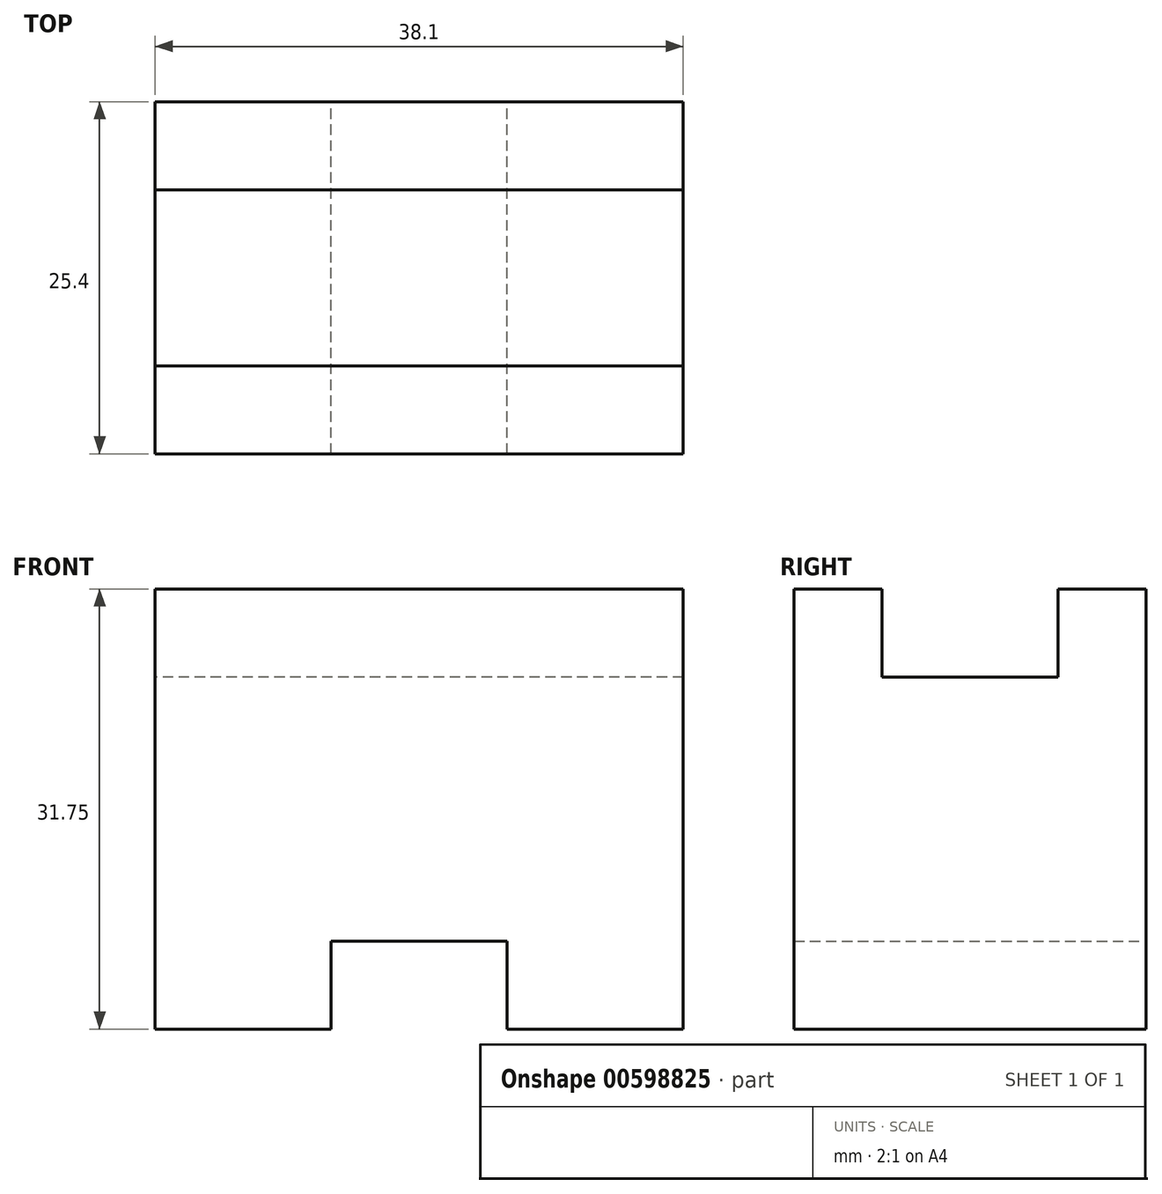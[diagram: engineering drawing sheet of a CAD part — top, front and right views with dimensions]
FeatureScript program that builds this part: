
annotation { "Feature Type Name" : "Feature", "Feature Type Description" : "" }
export const myFeature = defineFeature(function(context is Context, id is Id, definition is map)
    precondition{}
    {
        {
            var Q0;
            Q0=qCreatedBy(makeId("Front.planeOp"),FACE);
            var sketch = newSketch(context, id + "F0", { "sketchPlane" : qUnion([Q0])});
            skLineSegment(sketch, "E0", {"start": v(0, 0) * mm, "end": v(0, 31.75) * mm});
            skLineSegment(sketch, "E1", {"start": v(0, 31.75) * mm, "end": v(38.1, 31.75) * mm});
            skLineSegment(sketch, "E2", {"start": v(38.1, 31.75) * mm, "end": v(38.1, 0) * mm});
            skLineSegment(sketch, "E3", {"start": v(38.1, 0) * mm, "end": v(25.4, 0) * mm});
            skLineSegment(sketch, "E4", {"start": v(25.4, 0) * mm, "end": v(25.4, 6.35) * mm});
            skLineSegment(sketch, "E5", {"start": v(25.4, 6.35) * mm, "end": v(12.7, 6.35) * mm});
            skLineSegment(sketch, "E6", {"start": v(12.7, 6.35) * mm, "end": v(12.7, 0) * mm});
            skLineSegment(sketch, "E7", {"start": v(12.7, 0) * mm, "end": v(0, 0) * mm});
            skSolve(sketch);
        }
        {
            var Q0;
            Q0=makeQuery(id+"F0.imprint","IMPRINT",FACE,{"disambiguationData":[TD([[makeQuery(id+"F0.imprint","IMPRINT",EDGE,{"derivedFrom":sQuery(id+"F0.wireOp",EDGE,"E0")}),-1.0]])]});
            extrude(context, id + "F1", {"entities" : qUnion([Q0]), "depth" : 25.4 * mm, "offsetDistance" : 25.4 * mm});
        }
        {
            var Q0;
            Q0=makeQuery(id+"F1.opExtrude","SWEPT_FACE",FACE,{"disambiguationData":[OSD([sQuery(id+"F0.wireOp",EDGE,"E0")])]});
            var sketch = newSketch(context, id + "F2", { "sketchPlane" : qUnion([Q0])});
            skLineSegment(sketch, "E8", {"start": v(0, 31.75) * mm, "end": v(6.35, 31.75) * mm});
            skLineSegment(sketch, "E9", {"start": v(6.35, 31.75) * mm, "end": v(6.35, 25.4) * mm});
            skLineSegment(sketch, "E10", {"start": v(6.35, 25.4) * mm, "end": v(19.05, 25.4) * mm});
            skLineSegment(sketch, "E11", {"start": v(19.05, 25.4) * mm, "end": v(19.05, 31.75) * mm});
            skSolve(sketch);
        }
        {
            var Q0;
            Q0 = qSketchRegion(id + "F2", true);
            var Q1;
            {var subQ0=sQuery(id+"F2.wireOp",EDGE,"E9");Q1=makeQuery(id+"F2.imprint","IMPRINT",FACE,{"disambiguationData":[TD([[makeQuery(id+"F2.imprint","IMPRINT",EDGE,{"derivedFrom":subQ0}),1.0]])]});}
            extrude(context, id + "F3", {"entities" : qUnion([Q0, Q1]), "operationType" : NewBodyOperationType.REMOVE, "oppositeDirection" : true, "depth" : 38.1 * mm, "offsetDistance" : 25.4 * mm});
        }
    });
